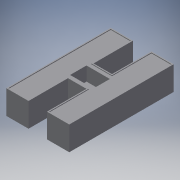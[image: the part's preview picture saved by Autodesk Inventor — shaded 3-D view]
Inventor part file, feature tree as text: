
AUTODESK INVENTOR PART (.ipt)
format: ipt  version: 2018.3 (Build 223284000, 284)  size: 274,432 bytes
history: native  units: mm
features: extrude x9, sketch x9, chamfer x5
ambient origin geometry x8: Origin, YZ Plane, XZ Plane, XY Plane, X Axis, Y Axis, Z Axis, Center Point
bodies: Solid1 (feature_tree)
feature tree (23):
  extrude  "Extrusion1"  Depth=19.2mm
  extrude  "Extrusion2"  Depth=15.87mm
  extrude  "Extrusion3"  Depth=34.0mm
  extrude  "Extrusion4"  Depth=6.9mm
  extrude  "Extrusion5"  Depth=27.15mm TaperAngle=0.0deg
  extrude  "Extrusion6"  Depth=14.549065mm
  extrude  "Extrusion7"  Depth=4.29mm TaperAngle=0.0deg
  extrude  "Extrusion8"  Depth=4.29mm
  extrude  "Extrusion9"  Depth=18.76mm TaperAngle=0.0deg
  chamfer  "Chamfer1"  Distance=16.68mm
  chamfer  "Chamfer2"  Distance=1.61mm
  chamfer  "Chamfer3"  Distance=2.877mm
  chamfer  "Chamfer4"  Distance=4.29mm
  chamfer  "Chamfer5"  Distance=88.14mm
  sketch  "Sketch1"  dims[d0=90.0mm d1=19.2mm]
  sketch  "Sketch2"  dims[d2=34.0mm d3=15.87mm]
  sketch  "Sketch3"  dims[d4=19.2mm d5=34.0mm]
  sketch  "Sketch4"  dims[d6=20.67mm d7=0.0mm d8=6.9mm]
  sketch  "Sketch5"  dims[d9=4.29mm d10=27.15mm d11=0.0mm]
  sketch  "Sketch6"  dims[d12=24.88mm d13=14.549065mm]
  sketch  "Sketch7"  dims[d14=2.877mm d15=4.29mm d16=0.0mm]
  sketch  "Sketch8"  dims[d17=6.9mm d18=4.29mm]
  sketch  "Sketch9"  dims[d19=4.48mm d20=18.76mm d21=0.0mm d22=16.68mm d23=1.61mm d24=2.877mm d25=4.29mm d26=0.0mm d27=88.14mm d28=17.34mm d29=34.0mm d30=17.73mm d31=34.0mm d32=17.34mm d33=88.14mm d34=34.0mm d35=0.62mm d36=0.0mm d37=22.0mm d38=0.93mm d39=0.93mm d40=14.1mm d41=20.1mm d42=3.02mm d43=3.02mm d44=16.15mm d45=16.16mm d46=12.0mm d47=0.0mm d48=11.0mm d49=2.6mm d50=5.7mm d51=4.5mm d52=12.0mm d53=0.0mm d54=15.2mm d55=34.0mm d56=90.0deg d57=19.87mm d58=34.0mm d59=15.2mm d60=86.0mm d61=15.2mm d62=34.0mm d63=90.0deg d64=18.0mm d65=0.0mm d66=2.0mm d67=2.0mm d68=45.0deg d69=2.0mm d70=2.0mm d71=45.0deg d72=2.0mm d73=2.0mm d74=45.0deg d75=2.0mm d76=2.0mm d77=45.0deg d78=2.0mm d79=2.0mm d80=45.0deg]
